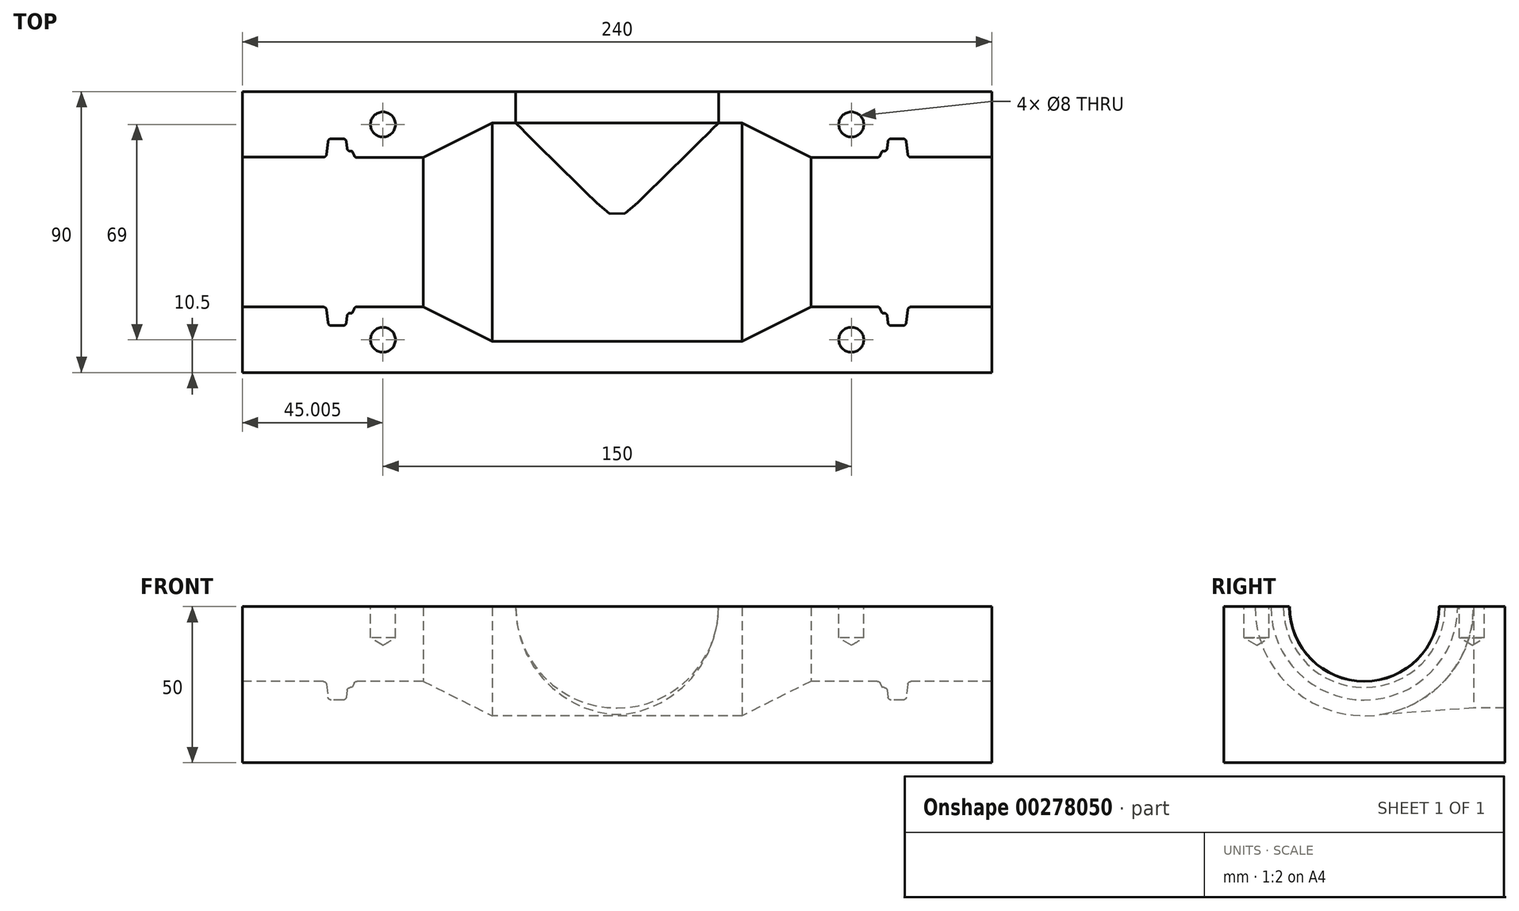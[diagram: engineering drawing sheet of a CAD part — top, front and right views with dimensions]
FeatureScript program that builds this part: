
annotation { "Feature Type Name" : "Feature", "Feature Type Description" : "" }
export const myFeature = defineFeature(function(context is Context, id is Id, definition is map)
    precondition{}
    {
        {
            var Q0;
            Q0=qCreatedBy(makeId("Top.planeOp"),FACE);
            var sketch = newSketch(context, id + "F0", { "sketchPlane" : qUnion([Q0])});
            skLineSegment(sketch, "E0", {"start": v(-15.3, 9.72) * mm, "end": v(24.7, 9.72) * mm});
            skLineSegment(sketch, "E1", {"start": v(24.7, 9.72) * mm, "end": v(44.7, -0.28) * mm});
            skLineSegment(sketch, "E2", {"start": v(76.3, 4.65) * mm, "end": v(72.45, 4.65) * mm});
            skLineSegment(sketch, "E3", {"start": v(70.18, 0.65) * mm, "end": v(69.7, 0.65) * mm});
            skLineSegment(sketch, "E4", {"start": v(77.17, 4.65) * mm, "end": v(77.17, 4.72) * mm});
            skLineSegment(sketch, "E5", {"start": v(-15.3, -25.28) * mm, "end": v(104.7, -25.28) * mm});
            skLineSegment(sketch, "E6", {"start": v(104.7, -25.28) * mm, "end": v(104.7, -1.28) * mm});
            skLineSegment(sketch, "E7", {"start": v(78.8, -1.28) * mm, "end": v(104.7, -1.28) * mm});
            skLineSegment(sketch, "E8", {"start": v(44.7, -0.28) * mm, "end": v(46.83, -1.35) * mm});
            skLineSegment(sketch, "E9", {"start": v(46.83, -1.35) * mm, "end": v(68.04, -1.35) * mm});
            skLineSegment(sketch, "E10", {"start": v(77.29, 3.77) * mm, "end": v(77.8, -0.4) * mm});
            skLineSegment(sketch, "E11", {"start": v(71.46, 3.78) * mm, "end": v(71.17, 1.52) * mm});
            skLineSegment(sketch, "E12", {"start": v(69.52, 0.54) * mm, "end": v(68.95, -0.75) * mm});
            skPoint(sketch, "E13.visualSharp", {"position": v(71.57, 4.65) * mm});
            skArc(sketch, "E13.filletArc", {"start": v(72.45, 4.65) * mm, "mid": v(71.79, 4.4) * mm, "end": v(71.46, 3.78) * mm});
            skPoint(sketch, "E14.newPointB", {"position": v(77.17, 4.65) * mm});
            skArc(sketch, "E14.filletArc", {"start": v(77.29, 3.77) * mm, "mid": v(76.96, 4.4) * mm, "end": v(76.3, 4.65) * mm});
            skPoint(sketch, "E15.visualSharp", {"position": v(77.9, -1.28) * mm});
            skArc(sketch, "E15.filletArc", {"start": v(77.8, -0.4) * mm, "mid": v(78.13, -1.03) * mm, "end": v(78.8, -1.28) * mm});
            skPoint(sketch, "E16.visualSharp", {"position": v(68.69, -1.35) * mm});
            skArc(sketch, "E16.filletArc", {"start": v(68.04, -1.35) * mm, "mid": v(68.58, -1.19) * mm, "end": v(68.95, -0.75) * mm});
            skPoint(sketch, "E17.visualSharp", {"position": v(71.05, 0.65) * mm});
            skArc(sketch, "E17.filletArc", {"start": v(70.18, 0.65) * mm, "mid": v(70.84, 0.9) * mm, "end": v(71.17, 1.52) * mm});
            skPoint(sketch, "E18.visualSharp", {"position": v(69.57, 0.65) * mm});
            skArc(sketch, "E18.filletArc", {"start": v(69.7, 0.65) * mm, "mid": v(69.6, 0.62) * mm, "end": v(69.52, 0.54) * mm});
            skArc(sketch, "E19.MirrorCS", {"start": v(-100.3, 0.65) * mm, "mid": v(-100.2, 0.62) * mm, "end": v(-100.13, 0.54) * mm});
            skLineSegment(sketch, "E20.MirrorCS", {"start": v(-100.79, 0.65) * mm, "end": v(-100.3, 0.65) * mm});
            skLineSegment(sketch, "E21.MirrorCS", {"start": v(-100.13, 0.54) * mm, "end": v(-99.56, -0.75) * mm});
            skArc(sketch, "E22.MirrorCS", {"start": v(-98.65, -1.35) * mm, "mid": v(-99.2, -1.19) * mm, "end": v(-99.56, -0.75) * mm});
            skLineSegment(sketch, "E23.MirrorCS", {"start": v(-102.07, 3.78) * mm, "end": v(-101.78, 1.52) * mm});
            skArc(sketch, "E24.MirrorCS", {"start": v(-100.79, 0.65) * mm, "mid": v(-101.45, 0.9) * mm, "end": v(-101.78, 1.52) * mm});
            skArc(sketch, "E25.MirrorCS", {"start": v(-107.9, 3.77) * mm, "mid": v(-107.57, 4.4) * mm, "end": v(-106.9, 4.65) * mm});
            skLineSegment(sketch, "E26.MirrorCS", {"start": v(-107.78, 4.65) * mm, "end": v(-107.78, 4.72) * mm});
            skLineSegment(sketch, "E27.MirrorCS", {"start": v(-106.9, 4.65) * mm, "end": v(-103.06, 4.65) * mm});
            skArc(sketch, "E28.MirrorCS", {"start": v(-103.06, 4.65) * mm, "mid": v(-102.4, 4.4) * mm, "end": v(-102.07, 3.78) * mm});
            skArc(sketch, "E29.MirrorCS", {"start": v(-108.41, -0.4) * mm, "mid": v(-108.74, -1.03) * mm, "end": v(-109.4, -1.28) * mm});
            skLineSegment(sketch, "E30.MirrorCS", {"start": v(-107.9, 3.77) * mm, "end": v(-108.41, -0.4) * mm});
            skLineSegment(sketch, "E31.MirrorCS", {"start": v(-75.3, -0.28) * mm, "end": v(-77.45, -1.35) * mm});
            skPoint(sketch, "E32.MirrorP", {"position": v(-101.67, 0.65) * mm});
            skPoint(sketch, "E33.MirrorP", {"position": v(-100.18, 0.65) * mm});
            skLineSegment(sketch, "E34.MirrorCS", {"start": v(-77.45, -1.35) * mm, "end": v(-98.65, -1.35) * mm});
            skLineSegment(sketch, "E35.MirrorCS", {"start": v(-55.3, 9.72) * mm, "end": v(-75.3, -0.28) * mm});
            skPoint(sketch, "E36.MirrorP", {"position": v(-102.18, 4.65) * mm});
            skPoint(sketch, "E37.MirrorP", {"position": v(-108.52, -1.28) * mm});
            skLineSegment(sketch, "E38.MirrorCS", {"start": v(-109.4, -1.28) * mm, "end": v(-135.3, -1.28) * mm});
            skLineSegment(sketch, "E39.MirrorCS", {"start": v(-15.3, -25.28) * mm, "end": v(-135.3, -25.28) * mm});
            skLineSegment(sketch, "E40.MirrorCS", {"start": v(-15.3, 9.72) * mm, "end": v(-55.3, 9.72) * mm});
            skPoint(sketch, "E41.MirrorP", {"position": v(-107.78, 4.65) * mm});
            skLineSegment(sketch, "E42.MirrorCS", {"start": v(-135.3, -25.28) * mm, "end": v(-135.3, -1.28) * mm});
            skPoint(sketch, "E43.MirrorP", {"position": v(-99.3, -1.35) * mm});
            skSolve(sketch);
        }
        {
            var Q0;
            Q0=qCreatedBy(makeId("Top.planeOp"),FACE);
            var sketch = newSketch(context, id + "F1", { "sketchPlane" : qUnion([Q0])});
            skLineSegment(sketch, "E44", {"start": v(-17.81, 9.72) * mm, "end": v(104.7, 9.72) * mm});
            skLineSegment(sketch, "E45", {"start": v(104.7, 9.72) * mm, "end": v(104.7, -25.28) * mm});
            skLineSegment(sketch, "E46", {"start": v(-135.3, -25.39) * mm, "end": v(-135.3, 9.72) * mm});
            skLineSegment(sketch, "E47", {"start": v(-135.3, 9.72) * mm, "end": v(-17.81, 9.72) * mm});
            skLineSegment(sketch, "E48.MirrorCS", {"start": v(-17.81, -60.28) * mm, "end": v(104.7, -60.28) * mm});
            skLineSegment(sketch, "E49.MirrorCS", {"start": v(-135.3, -60.28) * mm, "end": v(-17.81, -60.28) * mm});
            skLineSegment(sketch, "E50.MirrorCS", {"start": v(-135.3, -25.28) * mm, "end": v(-135.3, -60.28) * mm});
            skLineSegment(sketch, "E51.MirrorCS", {"start": v(104.7, -60.28) * mm, "end": v(104.7, -25.28) * mm});
            skSolve(sketch);
        }
        {
            var Q0;
            Q0 = qSketchRegion(id + "F1", true);
            extrude(context, id + "F2", {"entities" : qUnion([Q0]), "oppositeDirection" : true, "depth" : 50 * mm});
        }
        {
            var Q0;
            Q0=makeQuery(id+"F2.opExtrude","SWEPT_FACE",FACE,{"disambiguationData":[OSD([sQuery(id+"F1.wireOp",EDGE,"E48.MirrorCS"),sQuery(id+"F1.wireOp",EDGE,"E49.MirrorCS")])]});
            extrude(context, id + "F3", {"entities" : qUnion([Q0]), "operationType" : NewBodyOperationType.ADD, "depth" : 10 * mm});
        }
        {
            var Q0;
            Q0=makeQuery(id+"F2.opExtrude","SWEPT_FACE",FACE,{"disambiguationData":[OSD([sQuery(id+"F1.wireOp",EDGE,"E44"),sQuery(id+"F1.wireOp",EDGE,"E47")])]});
            extrude(context, id + "F4", {"entities" : qUnion([Q0]), "operationType" : NewBodyOperationType.ADD, "depth" : 10 * mm});
        }
        {
            var Q0;
            Q0=makeQuery(id+"F0.imprint","IMPRINT",FACE,{"disambiguationData":[TD([[makeQuery(id+"F0.imprint","IMPRINT",EDGE,{"derivedFrom":sQuery(id+"F0.wireOp",EDGE,"E0")}),-1.0]])]});
            var Q1;
            Q1=sQuery(id+"F0.wireOp",EDGE,"E39.MirrorCS");
            revolve(context, id + "F5", {"operationType" : NewBodyOperationType.REMOVE, "entities" : qUnion([Q0]), "axis" : qUnion([Q1]), "revolveType" : RevolveType.FULL, "oppositeDirection" : true});
        }
        {
            var Q0;
            {var subQ0=sQuery(id+"F1.wireOp",EDGE,"E50.MirrorCS");var subQ1=sQuery(id+"F1.wireOp",EDGE,"E49.MirrorCS");var subQ2=sQuery(id+"F1.wireOp",EDGE,"E51.MirrorCS");var subQ3=sQuery(id+"F1.wireOp",EDGE,"E45");var subQ4=sQuery(id+"F1.wireOp",EDGE,"E46");var subQ5=sQuery(id+"F1.wireOp",EDGE,"E44");var subQ6=sQuery(id+"F1.wireOp",EDGE,"E47");var subQ7=sQuery(id+"F1.wireOp",EDGE,"E48.MirrorCS");Q0=makeQuery(id+"F5.boolean.opBoolean","SPLIT",FACE,{"disambiguationData":[TD([makeQuery(id+"F4.opExtrude","CAP_FACE",FACE,{"disambiguationData":[OSD([subQ5,subQ6])],"isStart":false})])],"derivedFrom":makeQuery(id+"F4.boolean.opBoolean","MERGE",FACE,{"derivedFrom":[makeQuery(id+"F3.boolean.opBoolean","MERGE",FACE,{"derivedFrom":[makeQuery(id+"F2.opExtrude","CAP_FACE",FACE,{"disambiguationData":[OSD([subQ5,subQ3,subQ4,subQ6,subQ7,subQ1,subQ0,subQ2])],"isStart":true}),makeQuery(id+"F3.opExtrude","SWEPT_FACE",FACE,{"disambiguationData":[OSD([subQ7,subQ1]),TDD([makeQuery(id+"F2.opExtrude","CAP_EDGE",EDGE,{"disambiguationData":[OSD([subQ7,subQ1])],"isStart":true})])]})]}),makeQuery(id+"F4.opExtrude","SWEPT_FACE",FACE,{"disambiguationData":[OSD([subQ5,subQ6]),TDD([makeQuery(id+"F2.opExtrude","CAP_EDGE",EDGE,{"disambiguationData":[OSD([subQ5,subQ6])],"isStart":true})])]})]})});}
            var sketch = newSketch(context, id + "F6", { "sketchPlane" : qUnion([Q0])});
            skLineSegment(sketch, "E52", {"start": v(-15.3, 9.72) * mm, "end": v(-15.3, -25.28) * mm});
            skLineSegment(sketch, "E53", {"start": v(-15.3, -25.28) * mm, "end": v(-50.3, -25.28) * mm});
            skLineSegment(sketch, "E54", {"start": v(-47.8, 19.72) * mm, "end": v(-15.3, 19.72) * mm});
            skLineSegment(sketch, "E55", {"start": v(-15.3, 19.72) * mm, "end": v(-15.3, 9.72) * mm});
            skLineSegment(sketch, "E56", {"start": v(-47.8, 19.72) * mm, "end": v(-47.8, 9.72) * mm});
            skLineSegment(sketch, "E57", {"start": v(-47.8, 9.72) * mm, "end": v(-50.3, -25.28) * mm});
            skSolve(sketch);
        }
        {
            var Q0;
            Q0 = qSketchRegion(id + "F6", true);
            var Q1;
            Q1=sQuery(id+"F6.wireOp",EDGE,"E52");
            revolve(context, id + "F7", {"operationType" : NewBodyOperationType.REMOVE, "entities" : qUnion([Q0]), "axis" : qUnion([Q1]), "revolveType" : RevolveType.FULL, "oppositeDirection" : true});
        }
        {
            var Q0;
            {var subQ1=sQuery(id+"F1.wireOp",EDGE,"E50.MirrorCS");var subQ2=sQuery(id+"F1.wireOp",EDGE,"E46");var subQ9=sQuery(id+"F1.wireOp",EDGE,"E47");var subQ12=sQuery(id+"F1.wireOp",EDGE,"E49.MirrorCS");var subQ15=makeQuery(id+"F5.opRevolve","SWEPT_FACE",FACE,{"disambiguationData":[OSD([sQuery(id+"F0.wireOp",EDGE,"E19.MirrorCS")])]});var subQ16=sQuery(id+"F1.wireOp",EDGE,"E44");var subQ17=makeQuery(id+"F4.opExtrude","CAP_FACE",FACE,{"disambiguationData":[OSD([subQ16,subQ9])],"isStart":false});var subQ24=sQuery(id+"F1.wireOp",EDGE,"E51.MirrorCS");var subQ25=sQuery(id+"F1.wireOp",EDGE,"E45");var subQ26=sQuery(id+"F1.wireOp",EDGE,"E48.MirrorCS");Q0=makeQuery(id+"F7.boolean.opBoolean","SPLIT",FACE,{"disambiguationData":[TD([makeQuery(id+"F5.boolean.opBoolean","COPY",FACE,{"derivedFrom":subQ15})])],"derivedFrom":makeQuery(id+"F5.boolean.opBoolean","SPLIT",FACE,{"disambiguationData":[TD([subQ17])],"derivedFrom":makeQuery(id+"F4.boolean.opBoolean","MERGE",FACE,{"derivedFrom":[makeQuery(id+"F3.boolean.opBoolean","MERGE",FACE,{"derivedFrom":[makeQuery(id+"F2.opExtrude","CAP_FACE",FACE,{"disambiguationData":[OSD([subQ16,subQ25,subQ2,subQ9,subQ26,subQ12,subQ1,subQ24])],"isStart":true}),makeQuery(id+"F3.opExtrude","SWEPT_FACE",FACE,{"disambiguationData":[OSD([subQ26,subQ12]),TDD([makeQuery(id+"F2.opExtrude","CAP_EDGE",EDGE,{"disambiguationData":[OSD([subQ26,subQ12])],"isStart":true})])]})]}),makeQuery(id+"F4.opExtrude","SWEPT_FACE",FACE,{"disambiguationData":[OSD([subQ16,subQ9]),TDD([makeQuery(id+"F2.opExtrude","CAP_EDGE",EDGE,{"disambiguationData":[OSD([subQ16,subQ9])],"isStart":true})])]})]})})});}
            var sketch = newSketch(context, id + "F8", { "sketchPlane" : qUnion([Q0])});
            skLineSegment(sketch, "E58", {"start": v(-135.3, -59.78) * mm, "end": v(-90.3, -59.78) * mm});
            skLineSegment(sketch, "E59", {"start": v(-90.3, -59.78) * mm, "end": v(59.7, -59.78) * mm});
            skPoint(sketch, "E59.endSnap0", {"position": v(104.7, -59.78) * mm});
            skLineSegment(sketch, "E60", {"start": v(59.7, -59.78) * mm, "end": v(59.7, 9.22) * mm});
            skPoint(sketch, "E60.endSnap0", {"position": v(-135.3, 9.22) * mm});
            skLineSegment(sketch, "E61", {"start": v(59.7, 9.22) * mm, "end": v(-90.3, 9.22) * mm});
            skSolve(sketch);
        }
        {
            var Q0;
            Q0=sQuery(id+"F8.wireOp",VERTEX,"E61.end");
            var Q1;
            Q1=sQuery(id+"F8.wireOp",VERTEX,"E59.start");
            var Q2;
            Q2=sQuery(id+"F8.wireOp",VERTEX,"E60.start");
            var Q3;
            Q3=sQuery(id+"F8.wireOp",VERTEX,"E61.start");
            var Q4;
            Q4=makeQuery(id+"F2.opExtrude","SWEPT_BODY",BODY,{"disambiguationData":[OSD([sQuery(id+"F1.wireOp",EDGE,"E44"),sQuery(id+"F1.wireOp",EDGE,"E45"),sQuery(id+"F1.wireOp",EDGE,"E46"),sQuery(id+"F1.wireOp",EDGE,"E47"),sQuery(id+"F1.wireOp",EDGE,"E48.MirrorCS"),sQuery(id+"F1.wireOp",EDGE,"E49.MirrorCS"),sQuery(id+"F1.wireOp",EDGE,"E50.MirrorCS"),sQuery(id+"F1.wireOp",EDGE,"E51.MirrorCS")])]});
            hole(context, id + "F9", {"style" : HoleStyle.SIMPLE, "endStyle" : HoleEndStyle.BLIND, "holeDiameter" : 8 * mm, "holeDepth" : 10 * mm, "tappedDepth" : 12 * mm, "tapClearance" : 3, "startFromSketch" : true, "locations" : qUnion([Q0, Q1, Q2, Q3]), "scope" : qUnion([Q4])});
        }
    });
